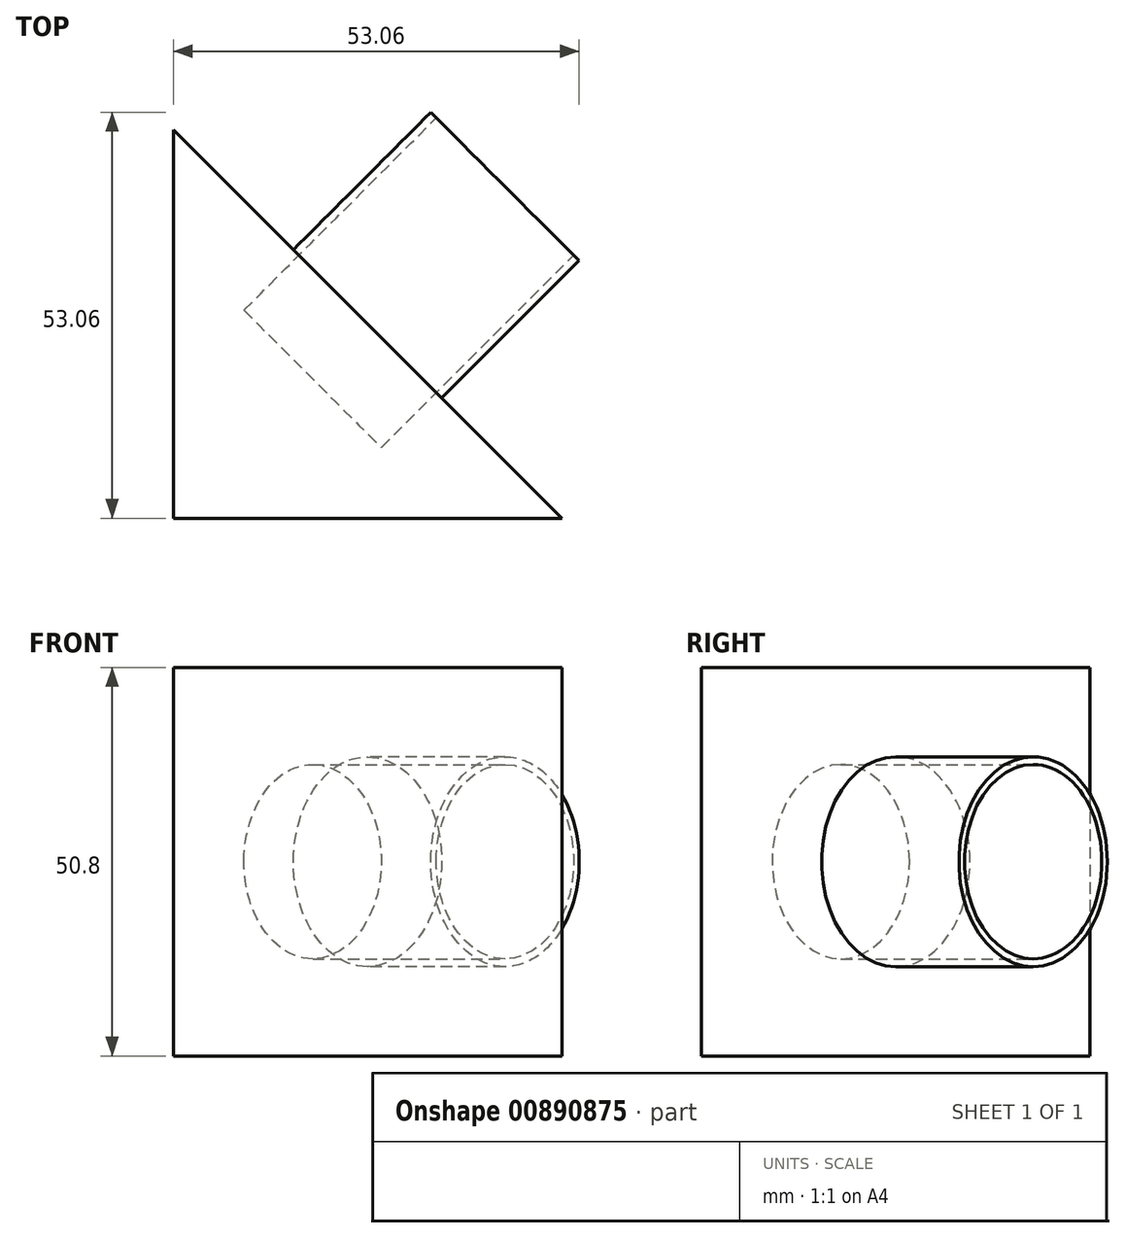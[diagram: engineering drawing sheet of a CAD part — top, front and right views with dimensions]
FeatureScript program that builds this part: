
annotation { "Feature Type Name" : "Feature", "Feature Type Description" : "" }
export const myFeature = defineFeature(function(context is Context, id is Id, definition is map)
    precondition{}
    {
        {
            var Q0;
            Q0=qCreatedBy(makeId("Top.planeOp"),FACE);
            var sketch = newSketch(context, id + "F0", { "sketchPlane" : qUnion([Q0])});
            skLineSegment(sketch, "E0.bottom", {"start": v(25.4, 25.4) * mm, "end": v(-25.4, 25.4) * mm});
            skLineSegment(sketch, "E0.top", {"start": v(25.4, -25.4) * mm, "end": v(-25.4, -25.4) * mm});
            skLineSegment(sketch, "E0.left", {"start": v(25.4, 25.4) * mm, "end": v(25.4, -25.4) * mm});
            skLineSegment(sketch, "E0.right", {"start": v(-25.4, 25.4) * mm, "end": v(-25.4, -25.4) * mm});
            skPoint(sketch, "E0.middle", {"position": v(0, 0) * mm});
            skLineSegment(sketch, "E1", {"start": v(-25.4, 25.4) * mm, "end": v(25.4, -25.4) * mm});
            skSolve(sketch);
        }
        {
            var Q0;
            Q0=makeQuery(id+"F0.imprint","IMPRINT",FACE,{"disambiguationData":[TD([[makeQuery(id+"F0.imprint","IMPRINT",EDGE,{"derivedFrom":sQuery(id+"F0.wireOp",EDGE,"E0.top")}),-1.0]])]});
            extrude(context, id + "F1", {"entities" : qUnion([Q0]), "depth" : 50.8 * mm, "offsetDistance" : 25.4 * mm});
        }
        {
            var Q0;
            Q0=makeQuery(id+"F1.opExtrude","SWEPT_FACE",FACE,{"disambiguationData":[OSD([sQuery(id+"F0.wireOp",EDGE,"E1")])]});
            var sketch = newSketch(context, id + "F2", { "sketchPlane" : qUnion([Q0])});
            skPoint(sketch, "E2.centerSnap0", {"position": v(35.92, 25.4) * mm});
            skPoint(sketch, "E2.centerSnap1", {"position": v(0, 50.8) * mm});
            skCircle(sketch, "E3", {"center": v(0, 25.4) * mm, "radius": 13.72 * mm});
            skSolve(sketch);
        }
        {
            var Q0;
            Q0 = qSketchRegion(id + "F2", true);
            extrude(context, id + "F3", {"entities" : qUnion([Q0]), "operationType" : NewBodyOperationType.ADD, "depth" : 25.4 * mm, "offsetDistance" : 25.4 * mm});
        }
        {
            var Q0;
            Q0=makeQuery(id+"F3.opExtrude","CAP_FACE",FACE,{"disambiguationData":[OSD([sQuery(id+"F2.wireOp",EDGE,"E3")])],"isStart":false});
            var sketch = newSketch(context, id + "F4", { "sketchPlane" : qUnion([Q0])});
            skCircle(sketch, "E4", {"center": v(0, 25.4) * mm, "radius": 12.7 * mm});
            skSolve(sketch);
        }
        {
            var Q0;
            Q0=makeQuery(id+"F4.imprint","IMPRINT",FACE,{"disambiguationData":[TD([[makeQuery(id+"F4.imprint","IMPRINT",EDGE,{"derivedFrom":sQuery(id+"F4.wireOp",EDGE,"E4")}),1.0]])]});
            extrude(context, id + "F5", {"entities" : qUnion([Q0]), "operationType" : NewBodyOperationType.REMOVE, "oppositeDirection" : true, "depth" : 35.56 * mm, "offsetDistance" : 25.4 * mm});
        }
    });
